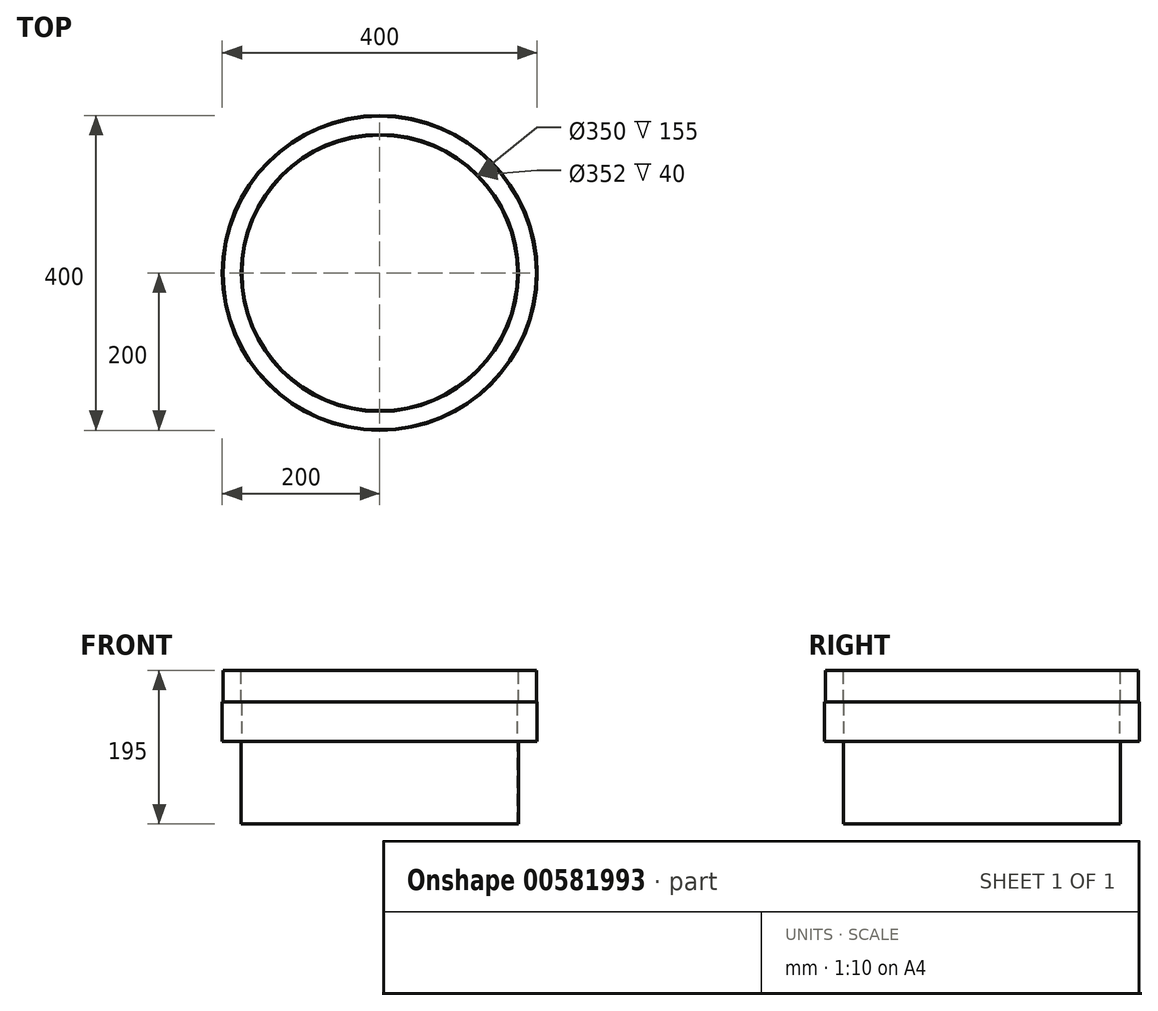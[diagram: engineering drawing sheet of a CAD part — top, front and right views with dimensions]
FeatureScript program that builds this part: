
annotation { "Feature Type Name" : "Feature", "Feature Type Description" : "" }
export const myFeature = defineFeature(function(context is Context, id is Id, definition is map)
    precondition{}
    {
        {
            var Q0;
            Q0=qCreatedBy(makeId("Front.planeOp"),FACE);
            var sketch = newSketch(context, id + "F0", { "sketchPlane" : qUnion([Q0])});
            skLineSegment(sketch, "E0", {"start": v(0, 710.75) * mm, "end": v(0, -704.58) * mm, "construction": true});
            skLineSegment(sketch, "E1", {"start": v(-175, 295.65) * mm, "end": v(-175, 410.65) * mm});
            skLineSegment(sketch, "E2", {"start": v(-175, 410.65) * mm, "end": v(-176, 410.65) * mm});
            skLineSegment(sketch, "E3", {"start": v(-199, 410.65) * mm, "end": v(-200, 410.65) * mm});
            skLineSegment(sketch, "E4", {"start": v(-200, 410.65) * mm, "end": v(-200, 360.65) * mm});
            skLineSegment(sketch, "E5", {"start": v(-200, 360.65) * mm, "end": v(-176, 360.65) * mm});
            skLineSegment(sketch, "E6", {"start": v(-176, 360.65) * mm, "end": v(-176, 295.65) * mm});
            skLineSegment(sketch, "E7", {"start": v(-199, 450.65) * mm, "end": v(-199, 410.65) * mm});
            skLineSegment(sketch, "E8", {"start": v(-199, 450.65) * mm, "end": v(-176, 450.65) * mm});
            skLineSegment(sketch, "E9", {"start": v(-176, 410.65) * mm, "end": v(-176, 450.65) * mm});
            skLineSegment(sketch, "E10", {"start": v(-175, 295.65) * mm, "end": v(-175, 255.65) * mm});
            skLineSegment(sketch, "E11", {"start": v(-176, 295.65) * mm, "end": v(-176, 255.65) * mm});
            skLineSegment(sketch, "E12", {"start": v(-176, 255.65) * mm, "end": v(-175, 255.65) * mm});
            skSolve(sketch);
        }
        {
            var Q0;
            Q0=qSketchRegion(id+"F0",true);
            var Q1;
            Q1=sQuery(id+"F0.wireOp",EDGE,"E0");
            revolve(context, id + "F1", {"entities" : qUnion([Q0]), "axis" : qUnion([Q1]), "revolveType" : RevolveType.FULL});
        }
    });
